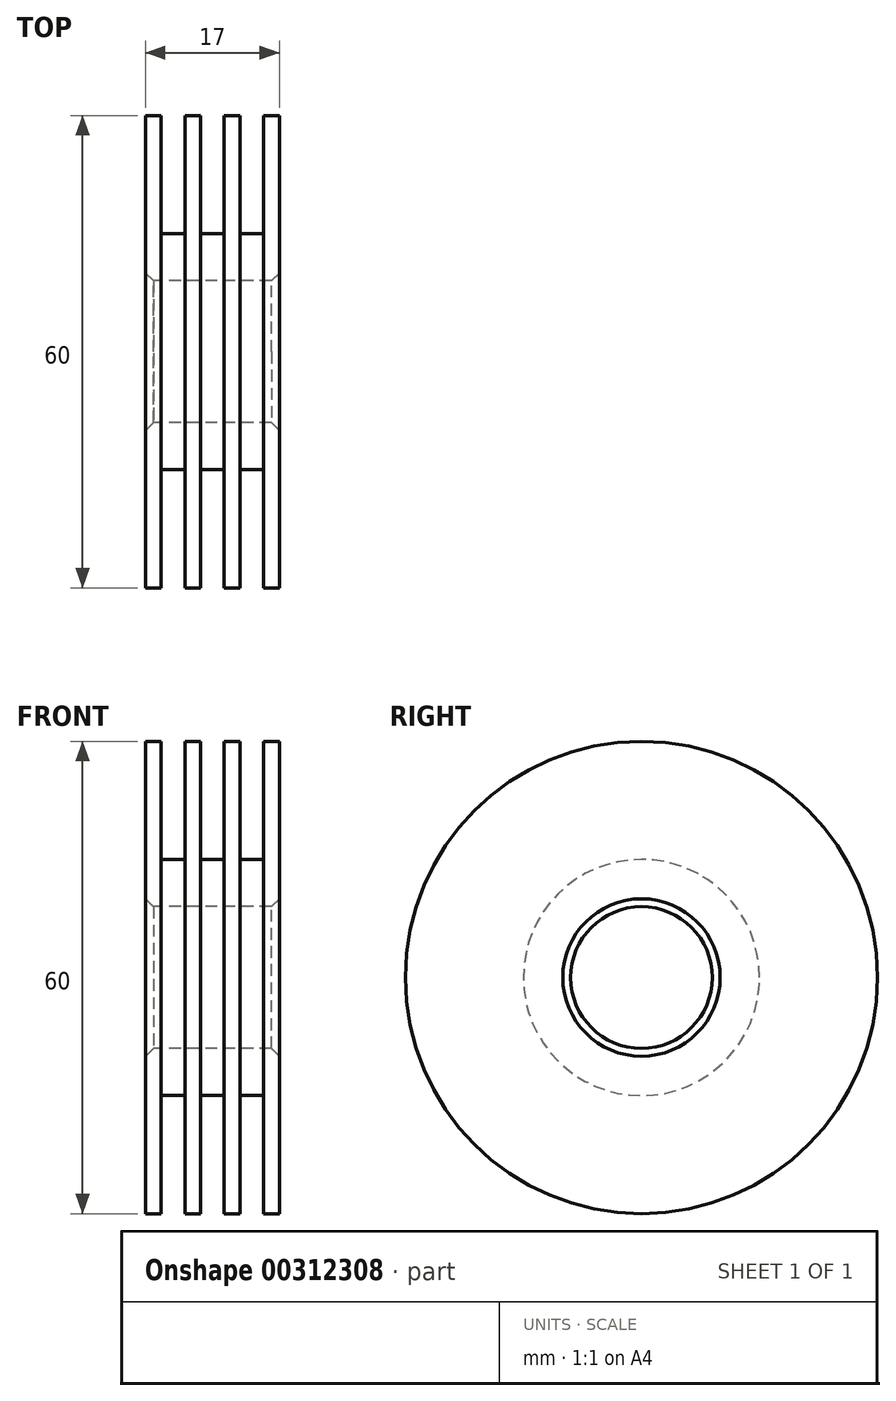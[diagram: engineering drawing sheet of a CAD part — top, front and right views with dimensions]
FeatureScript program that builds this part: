
annotation { "Feature Type Name" : "Feature", "Feature Type Description" : "" }
export const myFeature = defineFeature(function(context is Context, id is Id, definition is map)
    precondition{}
    {
        {
            var Q0;
            Q0=qCreatedBy(makeId("Front.planeOp"),FACE);
            var sketch = newSketch(context, id + "F0", { "sketchPlane" : qUnion([Q0])});
            skLineSegment(sketch, "E0", {"start": v(0, 0) * mm, "end": v(65.62, 0) * mm, "construction": true});
            skLineSegment(sketch, "E1", {"start": v(0, 9) * mm, "end": v(0, 30) * mm});
            skLineSegment(sketch, "E2", {"start": v(0, 30) * mm, "end": v(2, 30) * mm});
            skLineSegment(sketch, "E3", {"start": v(2, 30) * mm, "end": v(2, 15) * mm});
            skLineSegment(sketch, "E4", {"start": v(2, 15) * mm, "end": v(5, 15) * mm});
            skLineSegment(sketch, "E5", {"start": v(5, 15) * mm, "end": v(5, 30) * mm});
            skLineSegment(sketch, "E6", {"start": v(5, 30) * mm, "end": v(7, 30) * mm});
            skLineSegment(sketch, "E7", {"start": v(7, 30) * mm, "end": v(7, 15) * mm});
            skLineSegment(sketch, "E8", {"start": v(7, 15) * mm, "end": v(10, 15) * mm});
            skLineSegment(sketch, "E9", {"start": v(10, 15) * mm, "end": v(10, 30) * mm});
            skLineSegment(sketch, "E10", {"start": v(10, 30) * mm, "end": v(12, 30) * mm});
            skLineSegment(sketch, "E11", {"start": v(12, 30) * mm, "end": v(12, 15) * mm});
            skLineSegment(sketch, "E12", {"start": v(12, 15) * mm, "end": v(15, 15) * mm});
            skLineSegment(sketch, "E13", {"start": v(15, 15) * mm, "end": v(15, 30) * mm});
            skLineSegment(sketch, "E14", {"start": v(15, 30) * mm, "end": v(17, 30) * mm});
            skLineSegment(sketch, "E15", {"start": v(17, 30) * mm, "end": v(17, 9) * mm});
            skLineSegment(sketch, "E16", {"start": v(17, 9) * mm, "end": v(0, 9) * mm});
            skSolve(sketch);
        }
        {
            var Q0;
            Q0 = qSketchRegion(id + "F0", true);
            var Q1;
            Q1=sQuery(id+"F0.wireOp",EDGE,"E0");
            revolve(context, id + "F1", {"entities" : qUnion([Q0]), "axis" : qUnion([Q1]), "revolveType" : RevolveType.FULL});
        }
        {
            var Q0;
            Q0=makeQuery(id+"F1.opRevolve","SWEPT_EDGE",EDGE,{"disambiguationData":[OSD([sQuery(id+"F0.wireOp",EDGE,"E1"),sQuery(id+"F0.wireOp",EDGE,"E16")])]});
            var Q1;
            Q1=makeQuery(id+"F1.opRevolve","SWEPT_EDGE",EDGE,{"disambiguationData":[OSD([sQuery(id+"F0.wireOp",EDGE,"E15"),sQuery(id+"F0.wireOp",EDGE,"E16")])]});
            chamfer(context, id + "F2", {"entities" : qUnion([Q0, Q1]), "width" : 1 * mm, "tangentPropagation" : true});
        }
    });
